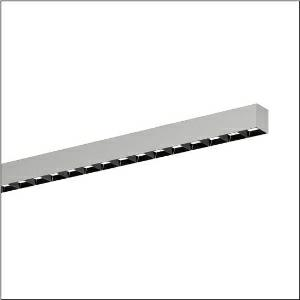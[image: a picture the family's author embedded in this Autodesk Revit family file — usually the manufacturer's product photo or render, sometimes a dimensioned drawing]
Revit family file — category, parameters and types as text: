
# Revit family: silica_21_51mx22dc3asb
name_source: partatom
category: Lighting Fixtures
units: mm (PartAtom-declared; Revit-internal decimal feet)

## family parameters
Cut with Voids When Loaded = No
Host = Face
Light Source = No
Part Type = Normal
Room Calculation Point = No
Round Connector Dimension = Use Diameter
Shared = No

## types (1)
- --- (1 x LED, 10800 lm, 69.2 W, 3000K)
    Apparent Load = 69 VA
    CIE Flux Codes = 86 100 100 100 100
    Color Rendering = 80
    Color Temperature = 3000K
    Default Elevation = 1800 mm
    Description = Silica 21, office luminaire, primary light control with darklight reflector, of PMMA, black, CAT 2 (L<= 3000cd/m²), light emission: direct distribution, primary light characteristic: symmetric, installation type: surface-mounted, LED, rated luminous flux: 10.800lm, luminous efficacy: 156lm/W, light colour: 830, colour temperature: 3000K, control gear: DALI 2, with terminal, 3+2-pole, max. 2.5mm², mains connection: 220..240V, AC, 50/60Hz, rated input power: 69.2W, luminaire housing, of aluminium, metallic grey (RAL 9006), length: 3.004mm, width: 53mm, height: 53mm, protection rating (complete): IP20, insulation class (complete): insulation class I (protective earthing), certification: CE, permissible operating ambient temperature: 0..+35°C, standard: EN 50419, packaging unit: 1 piece
    Height = 53 mm
    Lamp = 1 x LED
    Lamp Light Flux = 10800 lm
    Lamp Power = 69.2 W
    Lamp count = 1
    Length = 3004 mm
    Luminous efficacy = 156 lm/W
    Manufacturer = Siteco
    ModVariant = No
    Model = 51MX22DC3ASB
    Mounting Place = Ceiling
    Mounting Type = Surface mounted
    Number of Poles = 1
    OnlyDefault = Yes
    Power Factor = 1
    Product Name = Silica 21
    Product group = office luminaire | ceiling mounted
    ProductGroupID = 301
    Protection Class = Protection class I
    Protection Degree = IP 20
    RLX_Detail_Level = 1
    RLX_Emergency_Light_Flux = 0 lm
    RLX_Emergency_Type = 0
    RLX_Emergency_Type_DB = No
    RlxData = <blob elided: 64941 chars, md5=437c638b>
    Socket = socket
    Standby Power = 0 W
    System Light Flux = 10800 lm
    System Power = 69 W
    Type Comments = factory setting: luminous flux: 100 % | dim-lin: 254 | 392 mA
    Type Image = l_1335929.jpg
    URL = http://relux.com
    VarID = @adj_124671
    Voltage = 0 V
    Weight = 0.00 kg
    Width = 53 mm

## geometry (parser evidence)
native form markers: Blend x4, Sweep x9
no freeform markers — native parametric forms only
